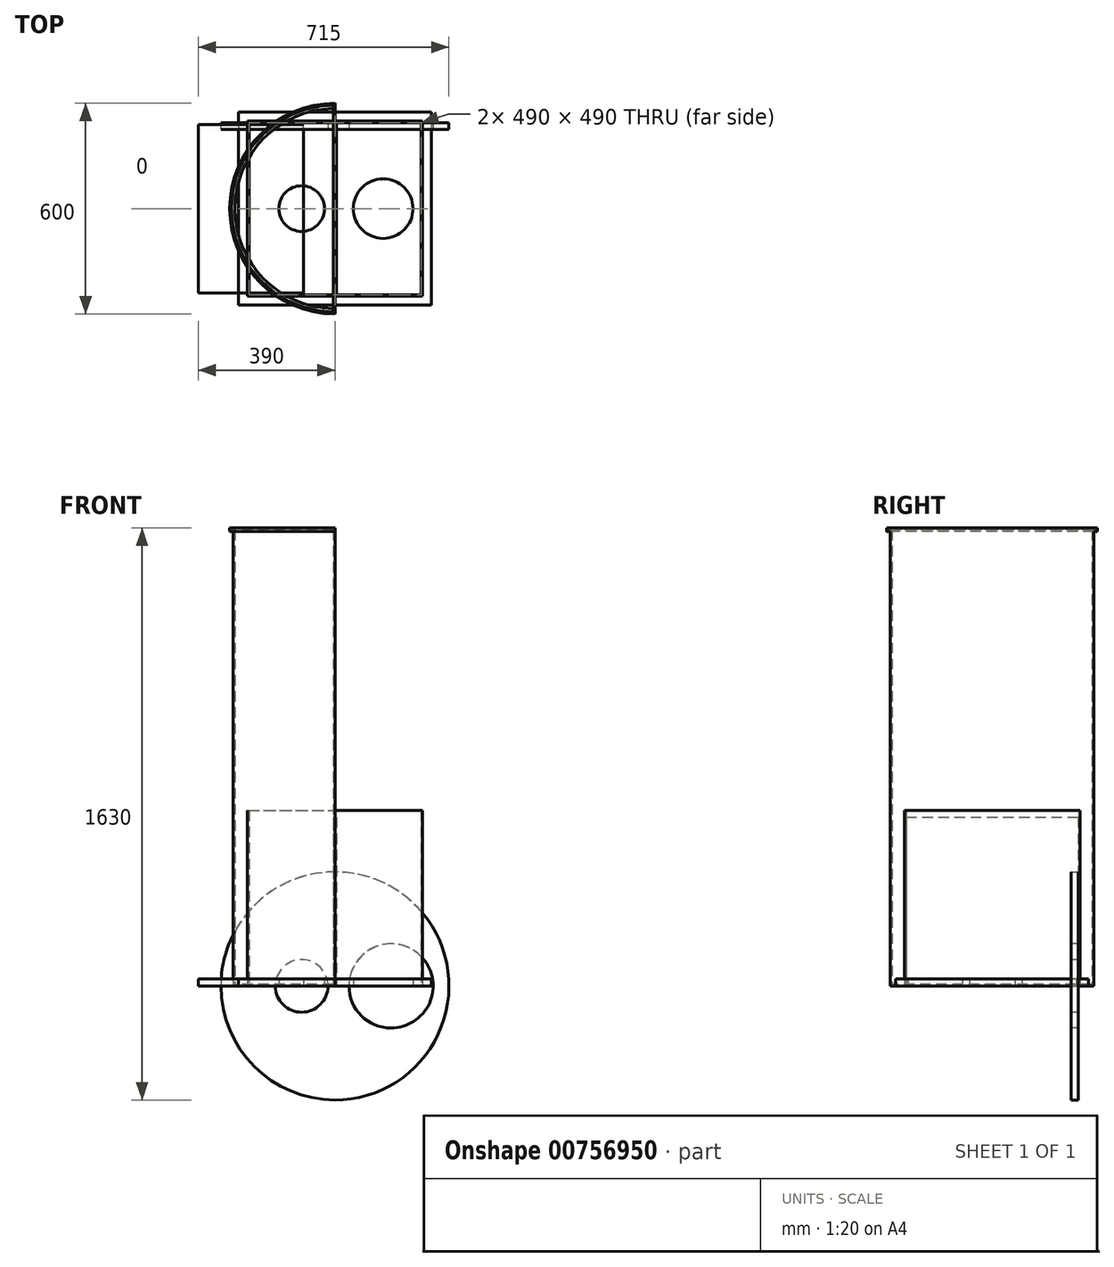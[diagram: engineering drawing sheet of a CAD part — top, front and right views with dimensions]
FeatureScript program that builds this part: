
annotation { "Feature Type Name" : "Feature", "Feature Type Description" : "" }
export const myFeature = defineFeature(function(context is Context, id is Id, definition is map)
    precondition{}
    {
        {
            var Q0;
            Q0=qCreatedBy(makeId("Top.planeOp"),FACE);
            var sketch = newSketch(context, id + "F0", { "sketchPlane" : qUnion([Q0])});
            skPoint(sketch, "E0", {"position": v(267.42, 0) * mm});
            skLineSegment(sketch, "E1.bottom", {"start": v(-250, 250) * mm, "end": v(250, 250) * mm});
            skLineSegment(sketch, "E1.top", {"start": v(-250, -250) * mm, "end": v(250, -250) * mm});
            skLineSegment(sketch, "E1.left", {"start": v(-250, 250) * mm, "end": v(-250, -250) * mm});
            skLineSegment(sketch, "E1.right", {"start": v(250, 250) * mm, "end": v(250, -250) * mm});
            skSolve(sketch);
        }
        {
            var Q0;
            Q0=makeQuery(id+"F0.imprint","IMPRINT",FACE,{"disambiguationData":[TD([[makeQuery(id+"F0.imprint","IMPRINT",EDGE,{"derivedFrom":sQuery(id+"F0.wireOp",EDGE,"E1.bottom")}),-1.0]])]});
            extrude(context, id + "F1", {"entities" : qUnion([Q0]), "depth" : 500 * mm, "offsetDistance" : 25.4 * mm});
        }
        {
            var Q0;
            Q0=makeQuery(id+"F1.opExtrude","CAP_FACE",FACE,{"disambiguationData":[OSD([sQuery(id+"F0.wireOp",EDGE,"E1.bottom"),sQuery(id+"F0.wireOp",EDGE,"E1.top"),sQuery(id+"F0.wireOp",EDGE,"E1.left"),sQuery(id+"F0.wireOp",EDGE,"E1.right")])],"isStart":false});
            var Q1;
            Q1=makeQuery(id+"F1.opExtrude","CAP_FACE",FACE,{"disambiguationData":[OSD([sQuery(id+"F0.wireOp",EDGE,"E1.bottom"),sQuery(id+"F0.wireOp",EDGE,"E1.top"),sQuery(id+"F0.wireOp",EDGE,"E1.left"),sQuery(id+"F0.wireOp",EDGE,"E1.right")])],"isStart":true});
            shell(context, id + "F2", {"entities" : qUnion([Q0, Q1]), "thickness" : 5 * mm});
        }
        {
            var Q0;
            Q0=qCreatedBy(makeId("Top.planeOp"),FACE);
            var sketch = newSketch(context, id + "F3", { "sketchPlane" : qUnion([Q0])});
            skLineSegment(sketch, "E2.bottom", {"start": v(5, 245) * mm, "end": v(-5, 245) * mm});
            skLineSegment(sketch, "E2.top", {"start": v(5, -245) * mm, "end": v(-5, -245) * mm});
            skLineSegment(sketch, "E2.left", {"start": v(5, 245) * mm, "end": v(5, -245) * mm});
            skLineSegment(sketch, "E2.right", {"start": v(-5, 245) * mm, "end": v(-5, -245) * mm});
            skSolve(sketch);
        }
        {
            var Q0;
            Q0 = qSketchRegion(id + "F3", true);
            extrude(context, id + "F4", {"entities" : qUnion([Q0]), "depth" : 480 * mm, "offsetDistance" : 25.4 * mm});
        }
        {
            var Q0;
            Q0=qCreatedBy(makeId("Top.planeOp"),FACE);
            var sketch = newSketch(context, id + "F5", { "sketchPlane" : qUnion([Q0])});
            skLineSegment(sketch, "E3", {"start": v(0, 290) * mm, "end": v(0, -290) * mm});
            skArc(sketch, "E4", {"start": v(0, 290) * mm, "mid": v(-290, 0) * mm, "end": v(0, -290) * mm});
            skSolve(sketch);
        }
        {
            var Q0;
            Q0=makeQuery(id+"F5.imprint","IMPRINT",FACE,{"disambiguationData":[TD([[makeQuery(id+"F5.imprint","IMPRINT",EDGE,{"derivedFrom":sQuery(id+"F5.wireOp",EDGE,"E3")}),-1.0]])]});
            extrude(context, id + "F6", {"entities" : qUnion([Q0]), "depth" : 1295 * mm, "offsetDistance" : 25.4 * mm});
        }
        {
            var Q0;
            Q0=makeQuery(id+"F6.opExtrude","CAP_FACE",FACE,{"disambiguationData":[OSD([sQuery(id+"F5.wireOp",EDGE,"E3"),sQuery(id+"F5.wireOp",EDGE,"E4")])],"isStart":false});
            var sketch = newSketch(context, id + "F7", { "sketchPlane" : qUnion([Q0])});
            skLineSegment(sketch, "E5", {"start": v(0, -300) * mm, "end": v(0, 300) * mm});
            skArc(sketch, "E6", {"start": v(0, 300) * mm, "mid": v(-300, 0) * mm, "end": v(0, -300) * mm});
            skSolve(sketch);
        }
        {
            var Q0;
            Q0 = qSketchRegion(id + "F7", true);
            extrude(context, id + "F8", {"entities" : qUnion([Q0]), "operationType" : NewBodyOperationType.ADD, "depth" : 10 * mm, "offsetDistance" : 25.4 * mm});
        }
        {
            var Q0;
            Q0=makeQuery(id+"F2.opShell","OFFSET_FACE",FACE,{"disambiguationData":[OSD([sQuery(id+"F0.wireOp",EDGE,"E1.bottom"),sQuery(id+"F0.wireOp",EDGE,"E1.top"),sQuery(id+"F0.wireOp",EDGE,"E1.left"),sQuery(id+"F0.wireOp",EDGE,"E1.right")])]});
            var sketch = newSketch(context, id + "F9", { "sketchPlane" : qUnion([Q0])});
            skCircle(sketch, "E7", {"center": v(0, 0) * mm, "radius": 325 * mm});
            skSolve(sketch);
        }
        {
            var Q0;
            Q0 = qSketchRegion(id + "F9", true);
            extrude(context, id + "F10", {"entities" : qUnion([Q0]), "depth" : 20 * mm, "offsetDistance" : 25.4 * mm});
        }
        {
            var Q0;
            Q0=makeQuery(id+"F10.opExtrude","CAP_FACE",FACE,{"disambiguationData":[OSD([sQuery(id+"F9.wireOp",EDGE,"E7")])],"isStart":false});
            var sketch = newSketch(context, id + "F11", { "sketchPlane" : qUnion([Q0])});
            skLineSegment(sketch, "E8", {"start": v(0, 0) * mm, "end": v(-95, 0) * mm});
            skLineSegment(sketch, "E9", {"start": v(0, 0) * mm, "end": v(160, 0) * mm});
            skCircle(sketch, "E10", {"center": v(-95, 0) * mm, "radius": 75 * mm});
            skCircle(sketch, "E11", {"center": v(160, 0) * mm, "radius": 120 * mm});
            skSolve(sketch);
        }
        {
            var Q0;
            Q0=sQuery(id+"F11.wireOp",VERTEX,"E11.center");
            var Q1;
            Q1=makeQuery(id+"F10.opExtrude","SWEPT_BODY",BODY,{"disambiguationData":[OSD([sQuery(id+"F9.wireOp",EDGE,"E7")])]});
            hole(context, id + "F12", {"style" : HoleStyle.SIMPLE, "endStyle" : HoleEndStyle.BLIND, "holeDiameter" : 240 * mm, "majorDiameter" : 6.35 * mm, "holeDepth" : 50 * mm, "isTappedThrough" : true, "tappedDepth" : 12.7 * mm, "tapClearance" : 3, "startFromSketch" : true, "locations" : qUnion([Q0]), "scope" : qUnion([Q1])});
        }
        {
            var Q0;
            Q0=sQuery(id+"F11.wireOp",VERTEX,"E8.end");
            var Q1;
            Q1=makeQuery(id+"F10.opExtrude","SWEPT_BODY",BODY,{"disambiguationData":[OSD([sQuery(id+"F9.wireOp",EDGE,"E7")])]});
            hole(context, id + "F13", {"style" : HoleStyle.SIMPLE, "endStyle" : HoleEndStyle.BLIND, "holeDiameter" : 150 * mm, "majorDiameter" : 6.35 * mm, "holeDepth" : 50 * mm, "isTappedThrough" : true, "tappedDepth" : 12.7 * mm, "tapClearance" : 3, "startFromSketch" : true, "locations" : qUnion([Q0]), "scope" : qUnion([Q1])});
        }
        {
            var Q0;
            Q0=qCreatedBy(makeId("Top.planeOp"),FACE);
            var sketch = newSketch(context, id + "F14", { "sketchPlane" : qUnion([Q0])});
            skLineSegment(sketch, "E12.bottom", {"start": v(-90, -240) * mm, "end": v(-390, -240) * mm});
            skLineSegment(sketch, "E12.top", {"start": v(-90, 240) * mm, "end": v(-390, 240) * mm});
            skLineSegment(sketch, "E12.left", {"start": v(-90, -240) * mm, "end": v(-90, 240) * mm});
            skLineSegment(sketch, "E12.right", {"start": v(-390, -240) * mm, "end": v(-390, 240) * mm});
            skSolve(sketch);
        }
        {
            var Q0;
            {var subQ3=sQuery(id+"F14.wireOp",EDGE,"E12.bottom");Q0=makeQuery(id+"F14.imprint","IMPRINT",FACE,{"disambiguationData":[TD([[makeQuery(id+"F14.imprint","IMPRINT",EDGE,{"derivedFrom":subQ3}),-1.0]])]});}
            extrude(context, id + "F15", {"entities" : qUnion([Q0]), "depth" : 20 * mm, "offsetDistance" : 25.4 * mm});
        }
        {
            var Q0;
            Q0=makeQuery(id+"F8.opExtrude","CAP_FACE",FACE,{"disambiguationData":[OSD([sQuery(id+"F7.wireOp",EDGE,"E5"),sQuery(id+"F7.wireOp",EDGE,"E6")])],"isStart":false});
            shell(context, id + "F16", {"entities" : qUnion([Q0]), "thickness" : 5 * mm});
        }
        {
            var Q0;
            Q0=qCreatedBy(makeId("Top.planeOp"),FACE);
            var sketch = newSketch(context, id + "F17", { "sketchPlane" : qUnion([Q0])});
            skLineSegment(sketch, "E13.bottom", {"start": v(-275, 275) * mm, "end": v(275, 275) * mm});
            skLineSegment(sketch, "E13.top", {"start": v(-275, -275) * mm, "end": v(275, -275) * mm});
            skLineSegment(sketch, "E13.left", {"start": v(-275, 275) * mm, "end": v(-275, -275) * mm});
            skLineSegment(sketch, "E13.right", {"start": v(275, 275) * mm, "end": v(275, -275) * mm});
            skLineSegment(sketch, "E14", {"start": v(0, 0) * mm, "end": v(-95, 0) * mm});
            skLineSegment(sketch, "E15", {"start": v(0, 0) * mm, "end": v(137.5, 0) * mm});
            skCircle(sketch, "E16", {"center": v(-95, 0) * mm, "radius": 65 * mm});
            skCircle(sketch, "E17", {"center": v(137.5, 0) * mm, "radius": 85 * mm});
            skSolve(sketch);
        }
        {
            var Q0;
            Q0=makeQuery(id+"F17.imprint","IMPRINT",FACE,{"disambiguationData":[TD([[makeQuery(id+"F17.imprint","IMPRINT",EDGE,{"derivedFrom":sQuery(id+"F17.wireOp",EDGE,"E13.bottom")}),-1.0]])]});
            extrude(context, id + "F18", {"entities" : qUnion([Q0]), "depth" : 20 * mm, "offsetDistance" : 25.4 * mm});
        }
    });
